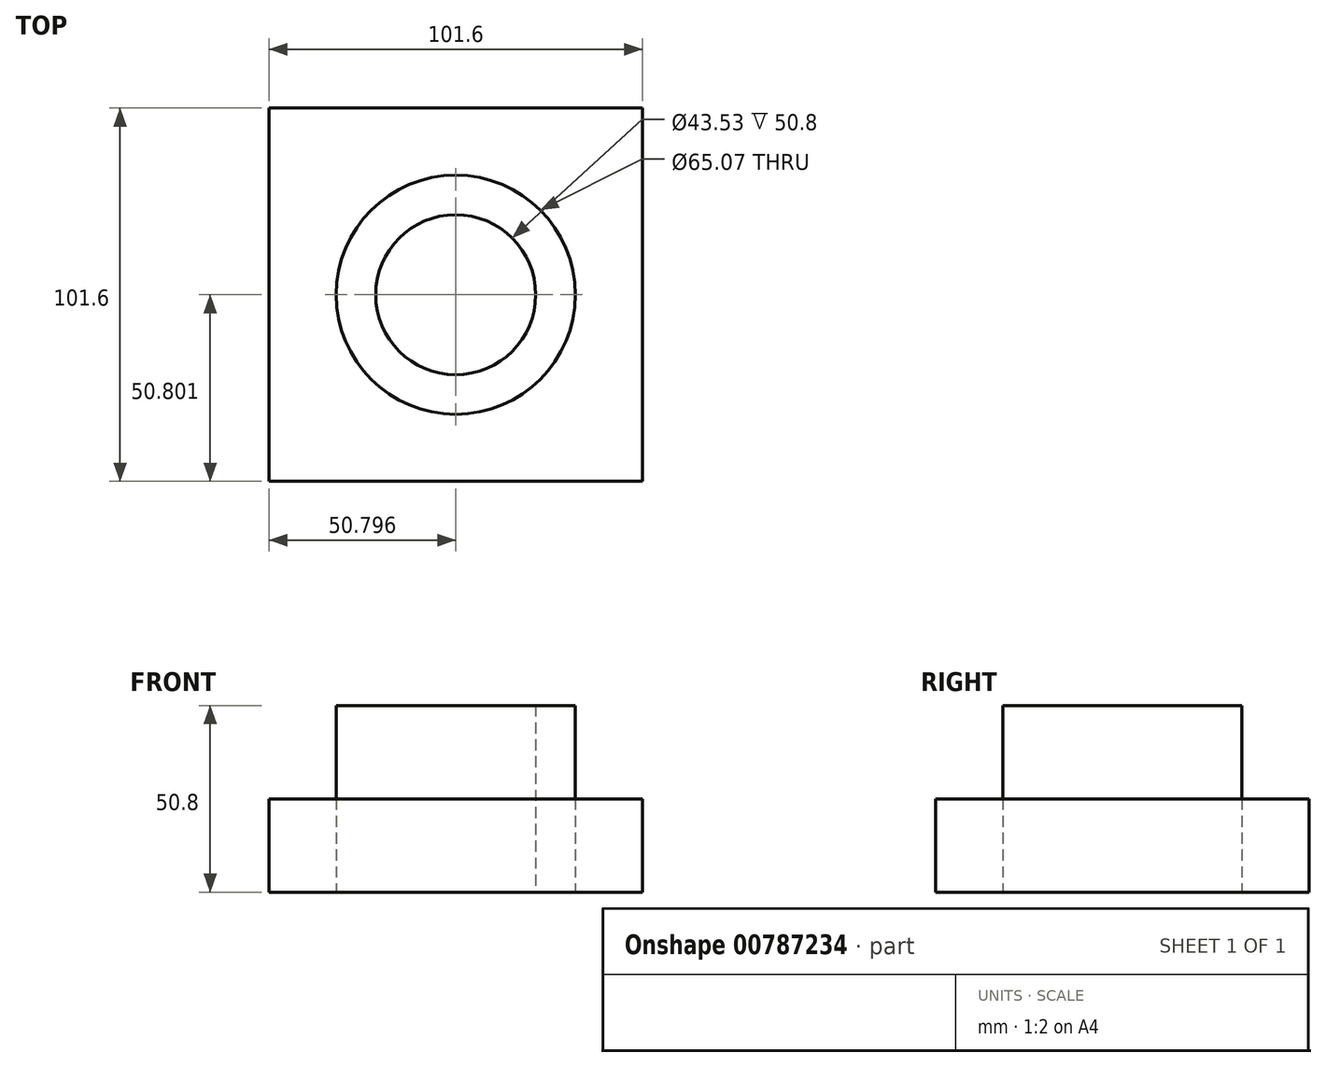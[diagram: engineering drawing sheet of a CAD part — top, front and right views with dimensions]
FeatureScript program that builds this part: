
annotation { "Feature Type Name" : "Feature", "Feature Type Description" : "" }
export const myFeature = defineFeature(function(context is Context, id is Id, definition is map)
    precondition{}
    {
        {
            var Q0;
            Q0=qCreatedBy(makeId("Top.planeOp"),FACE);
            var sketch = newSketch(context, id + "F0", { "sketchPlane" : qUnion([Q0])});
            skLineSegment(sketch, "E0", {"start": v(-45.54, 65.07) * mm, "end": v(56.06, 65.07) * mm});
            skLineSegment(sketch, "E1", {"start": v(56.06, -36.53) * mm, "end": v(56.06, 65.07) * mm});
            skLineSegment(sketch, "E2", {"start": v(56.06, -36.53) * mm, "end": v(-45.54, -36.53) * mm});
            skLineSegment(sketch, "E3", {"start": v(-45.54, -36.53) * mm, "end": v(-45.54, 65.07) * mm});
            skLineSegment(sketch, "E4", {"start": v(5.26, 65.07) * mm, "end": v(5.26, -36.53) * mm});
            skLineSegment(sketch, "E5", {"start": v(-45.54, 14.27) * mm, "end": v(56.06, 14.27) * mm});
            skCircle(sketch, "E6", {"center": v(5.26, 14.27) * mm, "radius": 32.54 * mm});
            skCircle(sketch, "E7", {"center": v(5.26, 14.27) * mm, "radius": 21.77 * mm});
            skSolve(sketch);
        }
        {
            var Q0;
            {var subQ1=sQuery(id+"F0.wireOp",EDGE,"E3");var subQ6=sQuery(id+"F0.wireOp",EDGE,"E0");var subQ9=makeQuery(id+"F0.imprint","INTERSECT",VERTEX,{"derivedFrom":[subQ6,subQ1]});Q0=makeQuery(id+"F0.imprint","IMPRINT",FACE,{"disambiguationData":[TD([[makeQuery(id+"F0.imprint","IMPRINT",EDGE,{"disambiguationData":[TD([[subQ9,-1.0]])],"derivedFrom":subQ6}),-1.0]])]});}
            var Q1;
            {var subQ1=sQuery(id+"F0.wireOp",EDGE,"E3");var subQ6=sQuery(id+"F0.wireOp",EDGE,"E2");var subQ9=makeQuery(id+"F0.imprint","INTERSECT",VERTEX,{"derivedFrom":[subQ6,subQ1]});Q1=makeQuery(id+"F0.imprint","IMPRINT",FACE,{"disambiguationData":[TD([[makeQuery(id+"F0.imprint","IMPRINT",EDGE,{"disambiguationData":[TD([[subQ9,1.0]])],"derivedFrom":subQ6}),-1.0]])]});}
            var Q2;
            {var subQ1=sQuery(id+"F0.wireOp",EDGE,"E2");var subQ5=sQuery(id+"F0.wireOp",EDGE,"E1");var subQ6=makeQuery(id+"F0.imprint","INTERSECT",VERTEX,{"derivedFrom":[subQ5,subQ1]});Q2=makeQuery(id+"F0.imprint","IMPRINT",FACE,{"disambiguationData":[TD([[makeQuery(id+"F0.imprint","IMPRINT",EDGE,{"disambiguationData":[TD([[subQ6,-1.0]])],"derivedFrom":subQ5}),1.0]])]});}
            var Q3;
            {var subQ1=sQuery(id+"F0.wireOp",EDGE,"E1");var subQ6=sQuery(id+"F0.wireOp",EDGE,"E0");var subQ9=makeQuery(id+"F0.imprint","INTERSECT",VERTEX,{"derivedFrom":[subQ6,subQ1]});Q3=makeQuery(id+"F0.imprint","IMPRINT",FACE,{"disambiguationData":[TD([[makeQuery(id+"F0.imprint","IMPRINT",EDGE,{"disambiguationData":[TD([[subQ9,1.0]])],"derivedFrom":subQ6}),-1.0]])]});}
            extrude(context, id + "F1", {"entities" : qUnion([Q0, Q1, Q2, Q3]), "depth" : 25.4 * mm, "offsetDistance" : 25.4 * mm});
        }
        {
            var Q0;
            {var subQ0=sQuery(id+"F0.wireOp",EDGE,"E6");var subQ1=sQuery(id+"F0.wireOp",EDGE,"E4");var subQ2=makeQuery(id+"F0.imprint","INTERSECT",VERTEX,{"disambiguationData":[OD(0.0)],"derivedFrom":[subQ1,subQ0]});Q0=makeQuery(id+"F0.imprint","IMPRINT",FACE,{"disambiguationData":[TD([[makeQuery(id+"F0.imprint","IMPRINT",EDGE,{"disambiguationData":[TD([[subQ2,-1.0]])],"derivedFrom":subQ1}),-1.0]])]});}
            var Q1;
            {var subQ0=sQuery(id+"F0.wireOp",EDGE,"E6");var subQ1=sQuery(id+"F0.wireOp",EDGE,"E4");var subQ2=makeQuery(id+"F0.imprint","INTERSECT",VERTEX,{"disambiguationData":[OD(0.0)],"derivedFrom":[subQ1,subQ0]});Q1=makeQuery(id+"F0.imprint","IMPRINT",FACE,{"disambiguationData":[TD([[makeQuery(id+"F0.imprint","IMPRINT",EDGE,{"disambiguationData":[TD([[subQ2,-1.0]])],"derivedFrom":subQ1}),1.0]])]});}
            var Q2;
            {var subQ0=sQuery(id+"F0.wireOp",EDGE,"E7");var subQ1=sQuery(id+"F0.wireOp",EDGE,"E4");var subQ2=makeQuery(id+"F0.imprint","INTERSECT",VERTEX,{"disambiguationData":[OD(1.0)],"derivedFrom":[subQ1,subQ0]});Q2=makeQuery(id+"F0.imprint","IMPRINT",FACE,{"disambiguationData":[TD([[makeQuery(id+"F0.imprint","IMPRINT",EDGE,{"disambiguationData":[TD([[subQ2,-1.0]])],"derivedFrom":subQ1}),1.0]])]});}
            var Q3;
            {var subQ0=sQuery(id+"F0.wireOp",EDGE,"E7");var subQ1=sQuery(id+"F0.wireOp",EDGE,"E4");var subQ2=makeQuery(id+"F0.imprint","INTERSECT",VERTEX,{"disambiguationData":[OD(1.0)],"derivedFrom":[subQ1,subQ0]});Q3=makeQuery(id+"F0.imprint","IMPRINT",FACE,{"disambiguationData":[TD([[makeQuery(id+"F0.imprint","IMPRINT",EDGE,{"disambiguationData":[TD([[subQ2,-1.0]])],"derivedFrom":subQ1}),-1.0]])]});}
            extrude(context, id + "F2", {"entities" : qUnion([Q0, Q1, Q2, Q3]), "depth" : 50.8 * mm, "offsetDistance" : 25.4 * mm});
        }
    });
